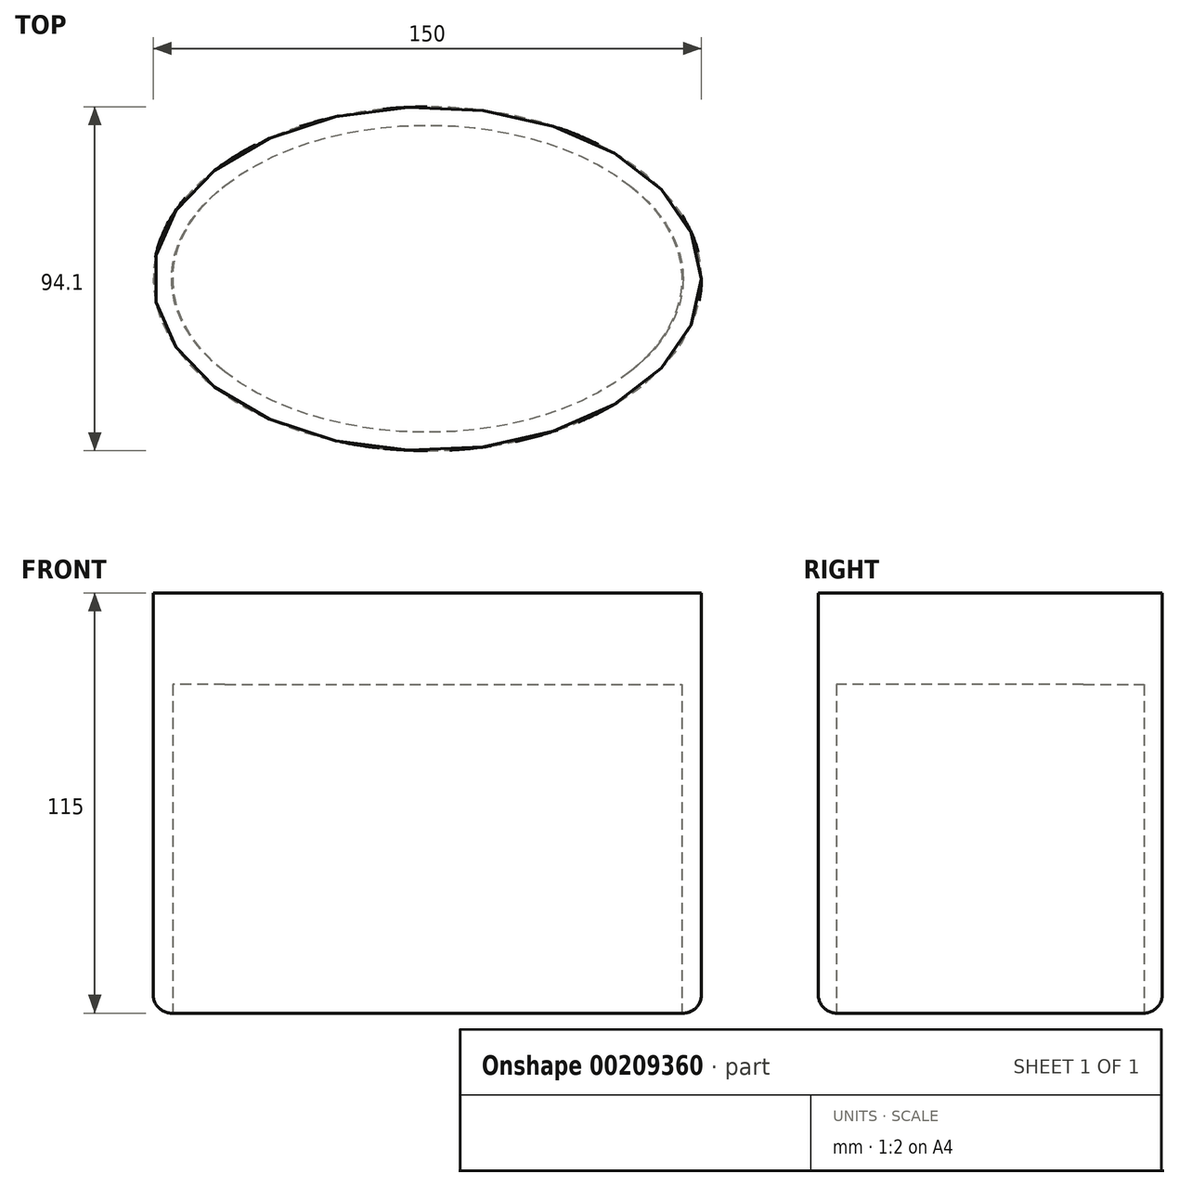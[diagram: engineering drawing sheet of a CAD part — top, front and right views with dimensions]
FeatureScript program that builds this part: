
annotation { "Feature Type Name" : "Feature", "Feature Type Description" : "" }
export const myFeature = defineFeature(function(context is Context, id is Id, definition is map)
    precondition{}
    {
        {
            var Q0;
            Q0=qCreatedBy(makeId("Top.planeOp"),FACE);
            var sketch = newSketch(context, id + "F0", { "sketchPlane" : qUnion([Q0])});
            skEllipse(sketch, "E0", {"center": v(0, 0) * mm, "majorRadius": 75 * mm, "minorRadius": 47.05 * mm, "majorAxis": v(1, 0)});
            skLineSegment(sketch, "E1", {"start": v(-33.25, 42.17) * mm, "end": v(-33.25, -42.17) * mm});
            skSolve(sketch);
        }
        {
            var Q0;
            Q0=makeQuery(id+"F0.imprint","IMPRINT",FACE,{"disambiguationData":[TD([[makeQuery(id+"F0.imprint","IMPRINT",EDGE,{"derivedFrom":sQuery(id+"F0.wireOp",EDGE,"E0")}),1.0]])]});
            extrude(context, id + "F1", {"entities" : qUnion([Q0]), "depth" : 90 * mm, "hasSecondDirection" : true, "secondDirectionOppositeDirection" : true, "secondDirectionDepth" : 25 * mm});
        }
        {
            var Q0;
            Q0=makeQuery(id+"F1.opExtrude","CAP_FACE",FACE,{"disambiguationData":[OSD([sQuery(id+"F0.wireOp",EDGE,"E0")])],"isStart":true});
            fillet(context, id + "F2", {"entities" : qUnion([Q0]), "radius" : 5 * mm, "tangentPropagation" : true, "allowEdgeOverflow" : false});
        }
        {
            var Q0;
            Q0=makeQuery(id+"F1.opExtrude","CAP_FACE",FACE,{"disambiguationData":[OSD([sQuery(id+"F0.wireOp",EDGE,"E0")])],"isStart":true});
            var sketch = newSketch(context, id + "F3", { "sketchPlane" : qUnion([Q0])});
            skEllipse(sketch, "E2", {"center": v(0, 0) * mm, "majorRadius": 69.62 * mm, "minorRadius": 42.14 * mm, "majorAxis": v(1, 0)});
            skSolve(sketch);
        }
        {
            var Q0;
            {var subQ0=sQuery(id+"F3.wireOp",EDGE,"E2");var subQ1=sQuery(id+"F0.wireOp",EDGE,"E0");var subQ2=makeQuery(id+"F2.opFillet","BLEND_EDGE",EDGE,{"blendedFrom":[makeQuery(id+"F1.opExtrude","CAP_EDGE",EDGE,{"disambiguationData":[OSD([subQ1])],"isStart":true}),makeQuery(id+"F1.opExtrude","CAP_FACE",FACE,{"disambiguationData":[OSD([subQ1])],"isStart":true})],"blendedInto":[makeQuery(id+"F1.opExtrude","CAP_FACE",FACE,{"disambiguationData":[OSD([subQ1])],"isStart":true})]});var subQ3=makeQuery(id+"F3.imprint","INTERSECT",VERTEX,{"disambiguationData":[OD(0.0)],"derivedFrom":[subQ2,subQ0]});Q0=makeQuery(id+"F3.imprint","IMPRINT",FACE,{"disambiguationData":[TD([[makeQuery(id+"F3.imprint","IMPRINT",EDGE,{"disambiguationData":[TD([[subQ3,-1.0]])],"derivedFrom":subQ0}),1.0]])]});}
            extrude(context, id + "F4", {"entities" : qUnion([Q0]), "operationType" : NewBodyOperationType.REMOVE, "oppositeDirection" : true, "depth" : 90 * mm});
        }
    });
